# Revit family: RA-DV_Double Angle_Right_DN10-15_Aero_RFA_1
name_source: partatom
category: Pipe Accessories
units: mm (PartAtom-declared; Revit-internal decimal feet)

## family parameters
Always vertical = Yes
Cut with Voids When Loaded = No
OmniClass Number = 23.65.55.14.17
OmniClass Title = Adjusting/Controlling Valves for Liquid Services
Part Type = Valve - Breaks Into
Round Connector Dimension = Use Diameter
Shared = No
Work Plane-Based = No

## types (2) — shared parameters
015G4540 = Aero Sensors_RA_RFA : Aero Sensors_Tamperproof_Built-in_7-28 °C_015G4540
015G4542 = Aero Sensors_RA_RFA : Aero Sensors_Tamperproof_Remote_7-26 °C_015G4542
015G4544 = Aero Sensors_RA_RFA : Aero Sensors_Tamperproof_Built-in_7-21 °C_015G4544
Application = 2-Pipe System
BH1 = 12 mm  [stored 0.0393701 ft]
BH2 = 9 mm  [stored 0.0295276 ft]
Description = Thermostatic Radiator Valve
HT = 21 mm
IfcExportAs = IfcValveType
IfcExportType = RA-DV
LL2 = 4 mm  [stored 0.0131234 ft]
LOD 200 = No
LOD 350 = Yes
Manufacturer = Danfoss
Max Differential Pressure = 0.6 bar
Max Flow (Text) = 135 l/h
Max Medium Temperature = 95 °C
Max Operating Pressure = 10 bar
Min Differential Pressure = 0.1 bar
Min Medium Temperature = 2 °C
RB1 = 12 mm  [stored 0.0393701 ft]
RB2 = 12 mm  [stored 0.0393701 ft]
RR1 = 10 mm  [stored 0.0328084 ft]
RR4 = 11 mm
RR5 = 8 mm  [stored 0.0262467 ft]
RT1 = 15 mm  [stored 0.0492126 ft]
RT5 = 15 mm  [stored 0.0492126 ft]
Sensor Type = Aero Sensors_RA_RFA : Aero Sensors_Built-in_7-28 °C
Setting Range = 1-7,N
TH1 = 10 mm  [stored 0.0328084 ft]
TH2 = 5 mm  [stored 0.0164042 ft]
TH3 = 6 mm  [stored 0.019685 ft]
TH4 = 7 mm  [stored 0.0229659 ft]
TH5 = 2 mm  [stored 0.00656168 ft]
TH6 = 13 mm
TH7 = 4 mm  [stored 0.0131234 ft]
TH8 = 4 mm  [stored 0.0131234 ft]
URL = https://store.danfoss.com
Valve Body Material = Danfoss Nickel Plated Brass
Ws = 56 mm  [stored 0.183727 ft]
Ws1 = 28 mm  [stored 0.0918635 ft]

## per-type parameters (varying)
| type | D | Hex | Hex2 | HexR1 | HexR2 | L | LL1 | LL3 | LL4 | LR1 | LR2 | Model | Model Type | RL1 | RL2 | RL4 | SA1 | SA2 | W | Weight |
| RA-DV_Double Angle_Right_DN10_013G7717 | 10 mm  [stored 0.0328084 ft] | 27 mm  [stored 0.0885827 ft] | 22 mm | 16 mm | 13 mm | 80 mm  [stored 0.262467 ft] | 21 mm | 9 mm  [stored 0.0295276 ft] | 19 mm | 16 mm | 11 mm | 013G7717 | RA-DV_Double Angle_Right_DN10 | 10 mm  [stored 0.0328084 ft] | 13 mm | 8 mm  [stored 0.0262467 ft] | 33 mm  [stored 0.108268 ft] | 27 mm  [stored 0.0885827 ft] | 55 mm | 0.28 kg |
| RA-DV_Double Angle_Right_DN15_013G7719 | 15 mm  [stored 0.0492126 ft] | 30 mm  [stored 0.0984252 ft] | 27 mm  [stored 0.0885827 ft] | 17 mm | 15 mm  [stored 0.0492126 ft] | 86 mm | 23 mm  [stored 0.0754593 ft] | 10 mm  [stored 0.0328084 ft] | 21 mm | 18 mm  [stored 0.0590551 ft] | 15 mm  [stored 0.0492126 ft] | 013G7719 | RA-DV_Double Angle_Right_DN15 | 11 mm | 15 mm  [stored 0.0492126 ft] | 11 mm | 37 mm | 33 mm  [stored 0.108268 ft] | 61 mm  [stored 0.200131 ft] | 0.33 kg |

note: [stored X ft] marks values corroborated as IEEE doubles in the binary element streams (Revit-internal decimal feet)

## geometry (parser evidence)
native form markers: Sweep x12
no freeform markers — native parametric forms only
